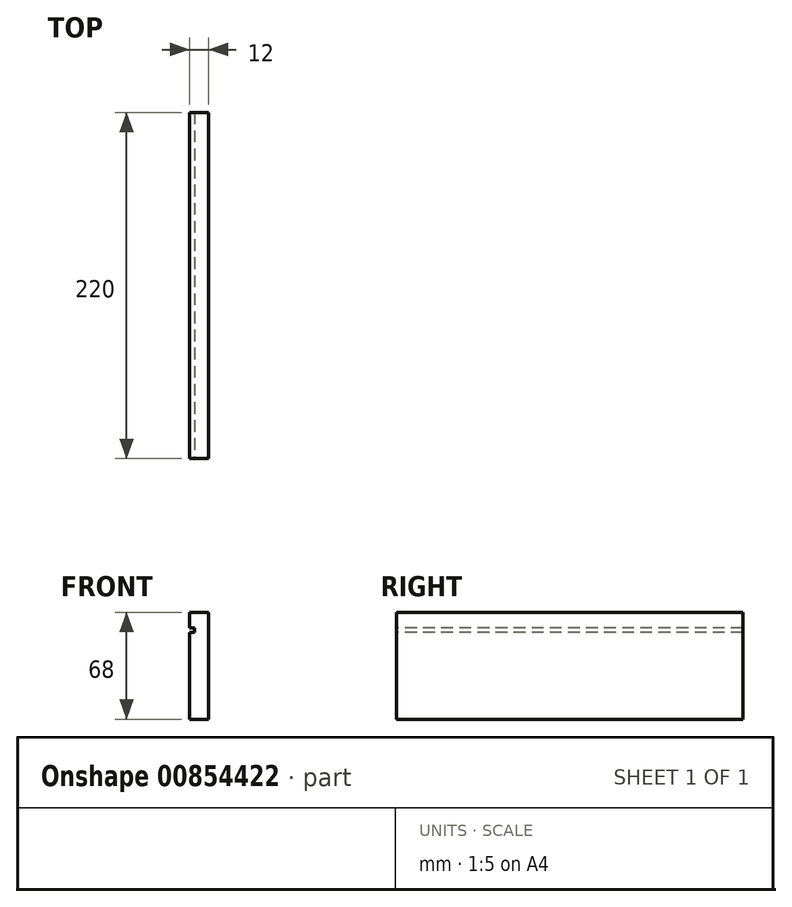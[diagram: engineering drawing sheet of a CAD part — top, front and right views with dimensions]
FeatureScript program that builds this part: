
annotation { "Feature Type Name" : "Feature", "Feature Type Description" : "" }
export const myFeature = defineFeature(function(context is Context, id is Id, definition is map)
    precondition{}
    {
        {
            var Q0;
            Q0=qCreatedBy(makeId("Right.planeOp"),FACE);
            var sketch = newSketch(context, id + "F0", { "sketchPlane" : qUnion([Q0])});
            skLineSegment(sketch, "E0.bottom", {"start": v(-110, 34) * mm, "end": v(110, 34) * mm});
            skLineSegment(sketch, "E0.top", {"start": v(-110, -34) * mm, "end": v(110, -34) * mm});
            skLineSegment(sketch, "E0.left", {"start": v(-110, 34) * mm, "end": v(-110, -34) * mm});
            skLineSegment(sketch, "E0.right", {"start": v(110, 34) * mm, "end": v(110, -34) * mm});
            skPoint(sketch, "E0.middle", {"position": v(0, 0) * mm});
            skSolve(sketch);
        }
        {
            var Q0;
            Q0 = qSketchRegion(id + "F0", true);
            extrude(context, id + "F1", {"entities" : qUnion([Q0]), "depth" : 12 * mm, "offsetDistance" : 25.4 * mm});
        }
        {
            var Q0;
            Q0=makeQuery(id+"F1.opExtrude","SWEPT_FACE",FACE,{"disambiguationData":[OSD([sQuery(id+"F0.wireOp",EDGE,"E0.left")])]});
            var sketch = newSketch(context, id + "F2", { "sketchPlane" : qUnion([Q0])});
            skLineSegment(sketch, "E1.bottom", {"start": v(0, 24) * mm, "end": v(3, 24) * mm});
            skLineSegment(sketch, "E1.top", {"start": v(0, 21) * mm, "end": v(3, 21) * mm});
            skLineSegment(sketch, "E1.left", {"start": v(0, 24) * mm, "end": v(0, 21) * mm});
            skLineSegment(sketch, "E1.right", {"start": v(3, 24) * mm, "end": v(3, 21) * mm});
            skSolve(sketch);
        }
        {
            var Q0;
            Q0=makeQuery(id+"F2.imprint","IMPRINT",FACE,{"disambiguationData":[TD([[makeQuery(id+"F2.imprint","IMPRINT",EDGE,{"derivedFrom":sQuery(id+"F2.wireOp",EDGE,"E1.bottom")}),-1.0]])]});
            extrude(context, id + "F3", {"entities" : qUnion([Q0]), "operationType" : NewBodyOperationType.REMOVE, "oppositeDirection" : true, "depth" : 500 * mm, "offsetDistance" : 25.4 * mm});
        }
    });
